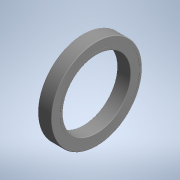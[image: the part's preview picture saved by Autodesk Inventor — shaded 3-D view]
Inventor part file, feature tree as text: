
AUTODESK INVENTOR PART (.ipt)
format: ipt  version: 2020 (Build 240168000, 168)  size: 157,184 bytes
history: native  units: mm (DEFAULTED — no unit token found)
features: other x21, revolve x1, sketch x1
ambient origin geometry x8: Origin, YZ Plane, XZ Plane, XY Plane, X Axis, Y Axis, Z Axis, Center Point
bodies: Solid1 (feature_tree)
feature tree (23):
  revolve  "Revolution1"  [1 undecoded]
  other  "center_point_XY"
  other  "center_point_YZ"
  other  "center_point_ZX"
  other  "center_point_X"
  other  "center_point_Y"
  other  "center_point_Z"
  other  "center_point_Center"
  other  "to_housing_XY"
  other  "to_housing_YZ"
  other  "to_housing_ZX"
  other  "to_housing_X"
  other  "to_housing_Y"
  other  "to_housing_Z"
  other  "to_housing_Center"
  other  "to_ring_XY"
  other  "to_ring_YZ"
  other  "to_ring_ZX"
  other  "to_ring_X"
  other  "to_ring_Y"
  other  "to_ring_Z"
  other  "to_ring_Center"
  sketch  "Sketch_1"  dims[d0=360.0deg d1=0.0mm]
note: 1 required parameter value undecoded (feature->parameter linkage not recoverable at this tier; creation-order binding heuristic only, values carry confidence <= 0.55)
